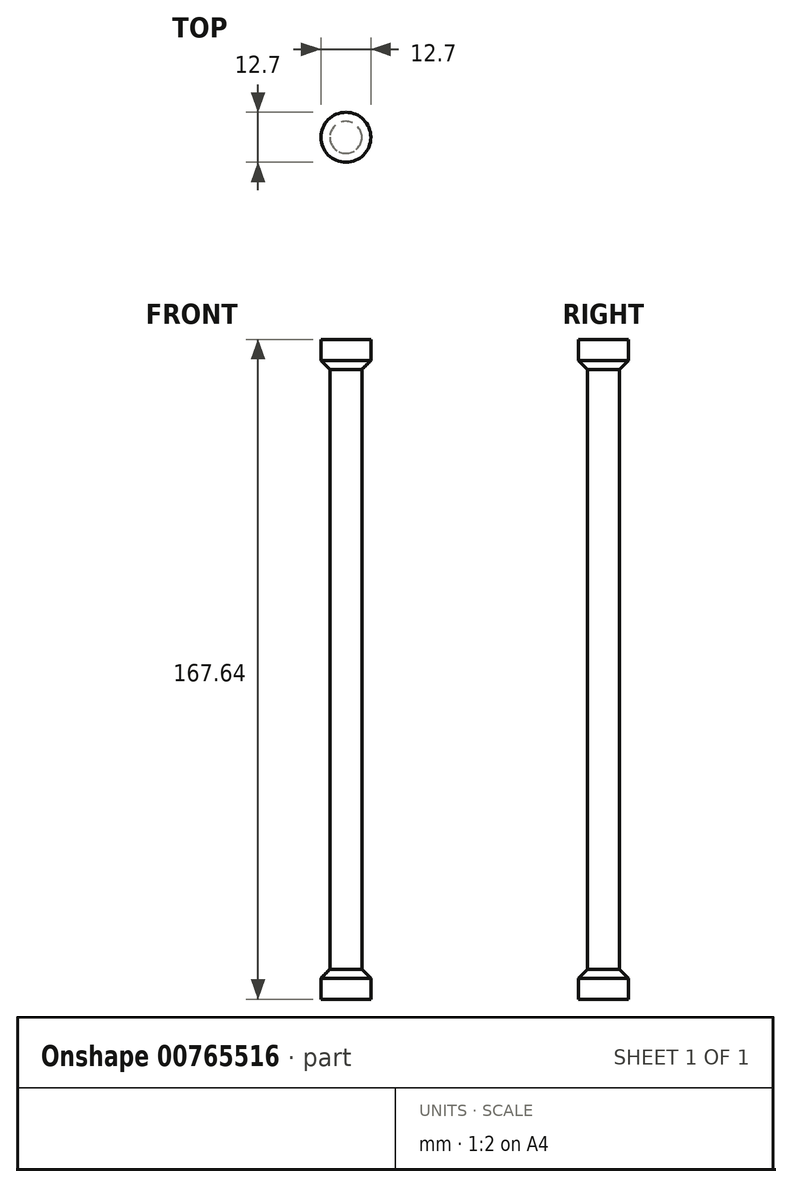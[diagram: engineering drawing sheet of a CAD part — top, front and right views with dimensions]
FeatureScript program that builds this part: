
annotation { "Feature Type Name" : "Feature", "Feature Type Description" : "" }
export const myFeature = defineFeature(function(context is Context, id is Id, definition is map)
    precondition{}
    {
        {
            var Q0;
            Q0=qCreatedBy(makeId("Top.planeOp"),FACE);
            var sketch = newSketch(context, id + "F0", { "sketchPlane" : qUnion([Q0])});
            skCircle(sketch, "E0", {"center": v(0, 0) * mm, "radius": 4.06 * mm});
            skSolve(sketch);
        }
        {
            var Q0;
            Q0=makeQuery(id+"F0.imprint","IMPRINT",FACE,{"disambiguationData":[TD([[makeQuery(id+"F0.imprint","IMPRINT",EDGE,{"derivedFrom":sQuery(id+"F0.wireOp",EDGE,"E0")}),1.0]])]});
            extrude(context, id + "F1", {"entities" : qUnion([Q0]), "depth" : 152.4 * mm, "offsetDistance" : 25.4 * mm});
        }
        {
            var Q0;
            Q0=makeQuery(id+"F1.opExtrude","CAP_FACE",FACE,{"disambiguationData":[OSD([sQuery(id+"F0.wireOp",EDGE,"E0")])],"isStart":false});
            var sketch = newSketch(context, id + "F2", { "sketchPlane" : qUnion([Q0])});
            skCircle(sketch, "E1", {"center": v(0, 0) * mm, "radius": 6.35 * mm});
            skSolve(sketch);
        }
        {
            var Q0;
            Q0=makeQuery(id+"F2.imprint","IMPRINT",FACE,{"disambiguationData":[TD([[makeQuery(id+"F2.imprint","IMPRINT",EDGE,{"derivedFrom":sQuery(id+"F2.wireOp",EDGE,"E1")}),1.0]])]});
            var Q1;
            Q1=makeQuery(id+"F2.imprint","IMPRINT",FACE,{"disambiguationData":[TD([[makeQuery(id+"F2.imprint","IMPRINT",EDGE,{"derivedFrom":makeQuery(id+"F1.opExtrude","CAP_EDGE",EDGE,{"disambiguationData":[OSD([sQuery(id+"F0.wireOp",EDGE,"E0")])],"isStart":false})}),1.0]])]});
            extrude(context, id + "F3", {"entities" : qUnion([Q0, Q1]), "operationType" : NewBodyOperationType.ADD, "depth" : 7.62 * mm, "offsetDistance" : 25.4 * mm});
        }
        {
            var Q0;
            Q0=makeQuery(id+"F1.opExtrude","CAP_FACE",FACE,{"disambiguationData":[OSD([sQuery(id+"F0.wireOp",EDGE,"E0")])],"isStart":true});
            var sketch = newSketch(context, id + "F4", { "sketchPlane" : qUnion([Q0])});
            skCircle(sketch, "E2", {"center": v(0, 0) * mm, "radius": 6.35 * mm});
            skSolve(sketch);
        }
        {
            var Q0;
            Q0=makeQuery(id+"F4.imprint","IMPRINT",FACE,{"disambiguationData":[TD([[makeQuery(id+"F4.imprint","IMPRINT",EDGE,{"derivedFrom":sQuery(id+"F4.wireOp",EDGE,"E2")}),1.0]])]});
            var Q1;
            Q1=makeQuery(id+"F4.imprint","IMPRINT",FACE,{"disambiguationData":[TD([[makeQuery(id+"F4.imprint","IMPRINT",EDGE,{"derivedFrom":makeQuery(id+"F1.opExtrude","CAP_EDGE",EDGE,{"disambiguationData":[OSD([sQuery(id+"F0.wireOp",EDGE,"E0")])],"isStart":true})}),-1.0]])]});
            extrude(context, id + "F5", {"entities" : qUnion([Q0, Q1]), "operationType" : NewBodyOperationType.ADD, "depth" : 7.62 * mm, "offsetDistance" : 25.4 * mm});
        }
        {
            var Q0;
            Q0=makeQuery(id+"F5.opExtrude","CAP_EDGE",EDGE,{"disambiguationData":[OSD([sQuery(id+"F4.wireOp",EDGE,"E2")])],"isStart":true});
            var Q1;
            Q1=makeQuery(id+"F3.opExtrude","CAP_EDGE",EDGE,{"disambiguationData":[OSD([sQuery(id+"F2.wireOp",EDGE,"E1")])],"isStart":true});
            chamfer(context, id + "F6", {"entities" : qUnion([Q0, Q1]), "width" : 2.3 * mm, "tangentPropagation" : true});
        }
    });
